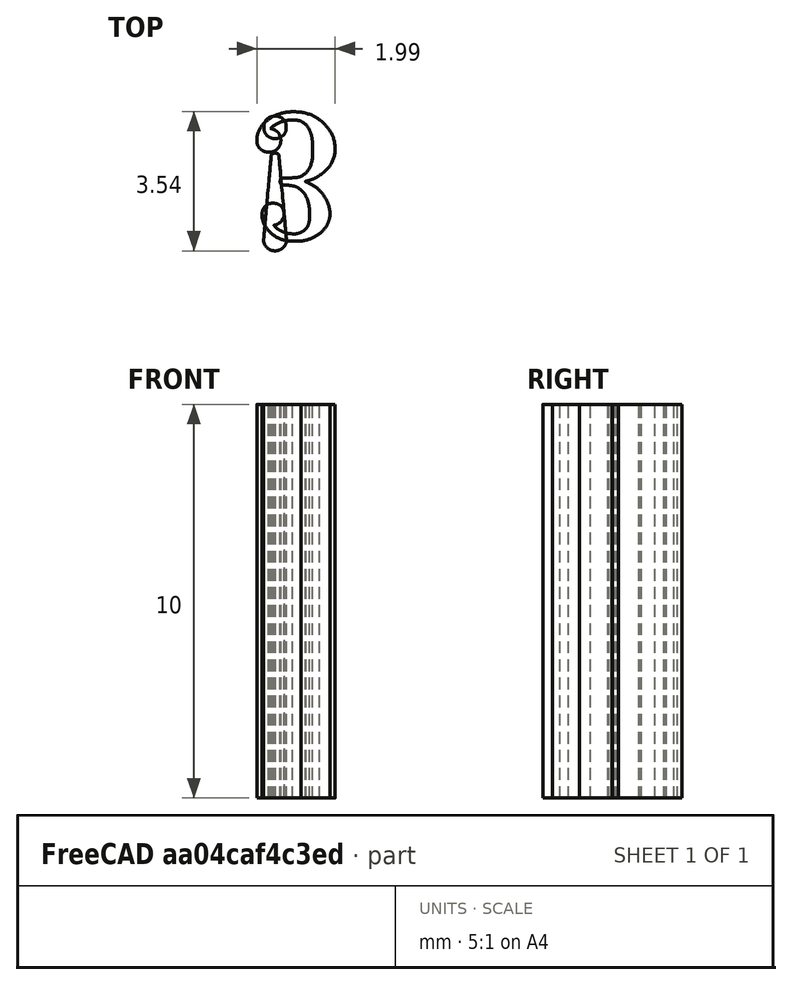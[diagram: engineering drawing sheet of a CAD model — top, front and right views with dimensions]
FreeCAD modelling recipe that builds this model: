
FCSTD DOCUMENT  (FreeCAD 0.19R)
Label: 6
License: All rights reserved
LicenseURL: http://en.wikipedia.org/wiki/All_rights_reserved
objects: Part::Feature×3, Sketcher::SketchObject×3, PartDesign::Pad×3, PartDesign::Body×3
note: 15 computed .brp shape members not serialized (recipe doc carries the construction recipe); baked Part::Feature solids carry a one-line shape summary decoded from their .brp

FEATURE [Part::Feature] MJX_12_TEX_N_33
  shape: bbox 1.987 x 3.29 x 2e-07 mm, 0 faces, 0 solids (baked)
FEATURE [Part::Feature] MJX_12_TEX_N_21
  shape: bbox 0.5794 x 2.48 x 2e-07 mm, 0 faces, 0 solids (baked)
FEATURE [Part::Feature] MJX_12_TEX_N_21001
  shape: bbox 0.5698 x 0.5746 x 2e-07 mm, 0 faces, 0 solids (baked)
FEATURE [Sketcher::SketchObject] Sketch
  FullyConstrained = false
  MapMode = 5
  Support = -> [XY_Plane]
  sketch-geometry (57):
    g0: BSplineCurve PolesCount=3 KnotsCount=2 Degree=2 IsPeriodic=0
    g1: BSplineCurve PolesCount=3 KnotsCount=2 Degree=2 IsPeriodic=0
    g2: BSplineCurve PolesCount=3 KnotsCount=2 Degree=2 IsPeriodic=0
    g3: BSplineCurve PolesCount=3 KnotsCount=2 Degree=2 IsPeriodic=0
    g4: BSplineCurve PolesCount=3 KnotsCount=2 Degree=2 IsPeriodic=0
    g5: BSplineCurve PolesCount=3 KnotsCount=2 Degree=2 IsPeriodic=0
    g6: BSplineCurve PolesCount=3 KnotsCount=2 Degree=2 IsPeriodic=0
    g7: BSplineCurve PolesCount=3 KnotsCount=2 Degree=2 IsPeriodic=0
    g8: BSplineCurve PolesCount=3 KnotsCount=2 Degree=2 IsPeriodic=0
    g9: BSplineCurve PolesCount=2 KnotsCount=2 Degree=1 IsPeriodic=0
    g10: BSplineCurve PolesCount=3 KnotsCount=2 Degree=2 IsPeriodic=0
    g11: BSplineCurve PolesCount=3 KnotsCount=2 Degree=2 IsPeriodic=0
    g12: BSplineCurve PolesCount=3 KnotsCount=2 Degree=2 IsPeriodic=0
    g13: BSplineCurve PolesCount=3 KnotsCount=2 Degree=2 IsPeriodic=0
    g14: BSplineCurve PolesCount=3 KnotsCount=2 Degree=2 IsPeriodic=0
    g15: BSplineCurve PolesCount=3 KnotsCount=2 Degree=2 IsPeriodic=0
    g16: BSplineCurve PolesCount=3 KnotsCount=2 Degree=2 IsPeriodic=0
    g17: BSplineCurve PolesCount=3 KnotsCount=2 Degree=2 IsPeriodic=0
    g18: BSplineCurve PolesCount=3 KnotsCount=2 Degree=2 IsPeriodic=0
    g19: BSplineCurve PolesCount=3 KnotsCount=2 Degree=2 IsPeriodic=0
    g20: BSplineCurve PolesCount=3 KnotsCount=2 Degree=2 IsPeriodic=0
    g21: BSplineCurve PolesCount=3 KnotsCount=2 Degree=2 IsPeriodic=0
    g22: BSplineCurve PolesCount=3 KnotsCount=2 Degree=2 IsPeriodic=0
    g23: BSplineCurve PolesCount=3 KnotsCount=2 Degree=2 IsPeriodic=0
    g24: BSplineCurve PolesCount=3 KnotsCount=2 Degree=2 IsPeriodic=0
    g25: BSplineCurve PolesCount=3 KnotsCount=2 Degree=2 IsPeriodic=0
    g26: BSplineCurve PolesCount=3 KnotsCount=2 Degree=2 IsPeriodic=0
    g27: BSplineCurve PolesCount=3 KnotsCount=2 Degree=2 IsPeriodic=0
    g28: BSplineCurve PolesCount=2 KnotsCount=2 Degree=1 IsPeriodic=0
    g29: BSplineCurve PolesCount=3 KnotsCount=2 Degree=2 IsPeriodic=0
    g30: BSplineCurve PolesCount=3 KnotsCount=2 Degree=2 IsPeriodic=0
    g31: BSplineCurve PolesCount=3 KnotsCount=2 Degree=2 IsPeriodic=0
    g32: BSplineCurve PolesCount=2 KnotsCount=2 Degree=1 IsPeriodic=0
    g33: BSplineCurve PolesCount=3 KnotsCount=2 Degree=2 IsPeriodic=0
    g34: BSplineCurve PolesCount=3 KnotsCount=2 Degree=2 IsPeriodic=0
    g35: BSplineCurve PolesCount=2 KnotsCount=2 Degree=1 IsPeriodic=0
    g36: BSplineCurve PolesCount=2 KnotsCount=2 Degree=1 IsPeriodic=0
    g37: BSplineCurve PolesCount=3 KnotsCount=2 Degree=2 IsPeriodic=0
    g38: BSplineCurve PolesCount=3 KnotsCount=2 Degree=2 IsPeriodic=0
    g39: BSplineCurve PolesCount=3 KnotsCount=2 Degree=2 IsPeriodic=0
    g40: BSplineCurve PolesCount=3 KnotsCount=2 Degree=2 IsPeriodic=0
    g41: BSplineCurve PolesCount=3 KnotsCount=2 Degree=2 IsPeriodic=0
    g42: BSplineCurve PolesCount=2 KnotsCount=2 Degree=1 IsPeriodic=0
    g43: BSplineCurve PolesCount=3 KnotsCount=2 Degree=2 IsPeriodic=0
    g44: BSplineCurve PolesCount=3 KnotsCount=2 Degree=2 IsPeriodic=0
    g45: BSplineCurve PolesCount=3 KnotsCount=2 Degree=2 IsPeriodic=0
    g46: BSplineCurve PolesCount=3 KnotsCount=2 Degree=2 IsPeriodic=0
    g47: BSplineCurve PolesCount=3 KnotsCount=2 Degree=2 IsPeriodic=0
    g48: BSplineCurve PolesCount=2 KnotsCount=2 Degree=1 IsPeriodic=0
    g49: BSplineCurve PolesCount=3 KnotsCount=2 Degree=2 IsPeriodic=0
    g50: BSplineCurve PolesCount=3 KnotsCount=2 Degree=2 IsPeriodic=0
    g51: BSplineCurve PolesCount=3 KnotsCount=2 Degree=2 IsPeriodic=0
    g52: BSplineCurve PolesCount=3 KnotsCount=2 Degree=2 IsPeriodic=0
    g53: BSplineCurve PolesCount=3 KnotsCount=2 Degree=2 IsPeriodic=0
    g54: BSplineCurve PolesCount=3 KnotsCount=2 Degree=2 IsPeriodic=0
    g55: BSplineCurve PolesCount=3 KnotsCount=2 Degree=2 IsPeriodic=0
    g56: BSplineCurve PolesCount=3 KnotsCount=2 Degree=2 IsPeriodic=0
  constraints (57):
    c: Coincident(g0,g1)
    c: Coincident(g1,g2)
    c: Coincident(g2,g3)
    c: Coincident(g3,g4)
    c: Coincident(g4,g5)
    c: Coincident(g5,g6)
    c: Coincident(g6,g7)
    c: Coincident(g7,g8)
    c: Coincident(g8,g9)
    c: Coincident(g9,g10)
    c: Coincident(g10,g11)
    c: Coincident(g11,g12)
    c: Coincident(g12,g13)
    c: Coincident(g13,g14)
    c: Coincident(g14,g15)
    c: Coincident(g15,g16)
    c: Coincident(g16,g17)
    c: Coincident(g17,g18)
    c: Coincident(g18,g19)
    c: Coincident(g19,g20)
    c: Coincident(g20,g21)
    c: Coincident(g21,g22)
    c: Coincident(g22,g23)
    c: Coincident(g23,g24)
    c: Coincident(g24,g25)
    c: Coincident(g25,g26)
    c: Coincident(g26,g27)
    c: Coincident(g27,g28)
    c: Coincident(g28,g29)
    c: Coincident(g29,g30)
    c: Coincident(g30,g31)
    c: Coincident(g31,g32)
    c: Coincident(g32,g33)
    c: Coincident(g33,g34)
    c: Coincident(g34,g35)
    c: Coincident(g35,g36)
    c: Coincident(g36,g37)
    c: Coincident(g37,g38)
    c: Coincident(g38,g39)
    c: Coincident(g39,g40)
    c: Coincident(g40,g41)
    c: Coincident(g41,g42)
    c: Coincident(g42,g43)
    c: Coincident(g43,g44)
    c: Coincident(g44,g45)
    c: Coincident(g45,g46)
    c: Coincident(g46,g47)
    c: Coincident(g47,g48)
    c: Coincident(g48,g49)
    c: Coincident(g49,g50)
    c: Coincident(g50,g51)
    c: Coincident(g51,g52)
    c: Coincident(g52,g53)
    c: Coincident(g53,g54)
    c: Coincident(g54,g55)
    c: Coincident(g55,g56)
    c: Coincident(g56,g0)
FEATURE [PartDesign::Pad] Pad
  Direction = (1,1,1)
  Length = 10
  Length2 = 100
  Profile = -> Sketch
  Type = 0
FEATURE [PartDesign::Body] Body
  Group = -> [Sketch,Pad]
  Origin = -> Origin
  Tip = -> Pad
FEATURE [Sketcher::SketchObject] Sketch001
  FullyConstrained = false
  MapMode = 5
  Support = -> [XY_Plane001]
  sketch-geometry (10):
    g0: BSplineCurve PolesCount=3 KnotsCount=2 Degree=2 IsPeriodic=0
    g1: BSplineCurve PolesCount=3 KnotsCount=2 Degree=2 IsPeriodic=0
    g2: BSplineCurve PolesCount=3 KnotsCount=2 Degree=2 IsPeriodic=0
    g3: BSplineCurve PolesCount=3 KnotsCount=2 Degree=2 IsPeriodic=0
    g4: BSplineCurve PolesCount=3 KnotsCount=2 Degree=2 IsPeriodic=0
    g5: BSplineCurve PolesCount=3 KnotsCount=2 Degree=2 IsPeriodic=0
    g6: BSplineCurve PolesCount=3 KnotsCount=2 Degree=2 IsPeriodic=0
    g7: BSplineCurve PolesCount=3 KnotsCount=2 Degree=2 IsPeriodic=0
    g8: BSplineCurve PolesCount=3 KnotsCount=2 Degree=2 IsPeriodic=0
    g9: BSplineCurve PolesCount=3 KnotsCount=2 Degree=2 IsPeriodic=0
  constraints (10):
    c: Coincident(g0,g1)
    c: Coincident(g1,g2)
    c: Coincident(g2,g3)
    c: Coincident(g3,g4)
    c: Coincident(g4,g5)
    c: Coincident(g5,g6)
    c: Coincident(g6,g7)
    c: Coincident(g7,g8)
    c: Coincident(g8,g9)
    c: Coincident(g9,g0)
FEATURE [Sketcher::SketchObject] Sketch002
  FullyConstrained = false
  MapMode = 5
  Support = -> [XY_Plane002]
  sketch-geometry (8):
    g0: BSplineCurve PolesCount=3 KnotsCount=2 Degree=2 IsPeriodic=0
    g1: BSplineCurve PolesCount=3 KnotsCount=2 Degree=2 IsPeriodic=0
    g2: BSplineCurve PolesCount=3 KnotsCount=2 Degree=2 IsPeriodic=0
    g3: BSplineCurve PolesCount=3 KnotsCount=2 Degree=2 IsPeriodic=0
    g4: BSplineCurve PolesCount=3 KnotsCount=2 Degree=2 IsPeriodic=0
    g5: BSplineCurve PolesCount=3 KnotsCount=2 Degree=2 IsPeriodic=0
    g6: BSplineCurve PolesCount=3 KnotsCount=2 Degree=2 IsPeriodic=0
    g7: BSplineCurve PolesCount=3 KnotsCount=2 Degree=2 IsPeriodic=0
  constraints (8):
    c: Coincident(g0,g1)
    c: Coincident(g1,g2)
    c: Coincident(g2,g3)
    c: Coincident(g3,g4)
    c: Coincident(g4,g5)
    c: Coincident(g5,g6)
    c: Coincident(g6,g7)
    c: Coincident(g7,g0)
FEATURE [PartDesign::Pad] Pad001
  Direction = (1,1,1)
  Length = 10
  Length2 = 100
  Profile = -> Sketch001
  Type = 0
FEATURE [PartDesign::Body] Body001
  Group = -> [Sketch001,Pad001]
  Origin = -> Origin001
  Tip = -> Pad001
FEATURE [PartDesign::Pad] Pad002
  Direction = (1,1,1)
  Length = 10
  Length2 = 100
  Profile = -> Sketch002
  Type = 0
FEATURE [PartDesign::Body] Body002
  Group = -> [Sketch002,Pad002]
  Origin = -> Origin002
  Tip = -> Pad002
